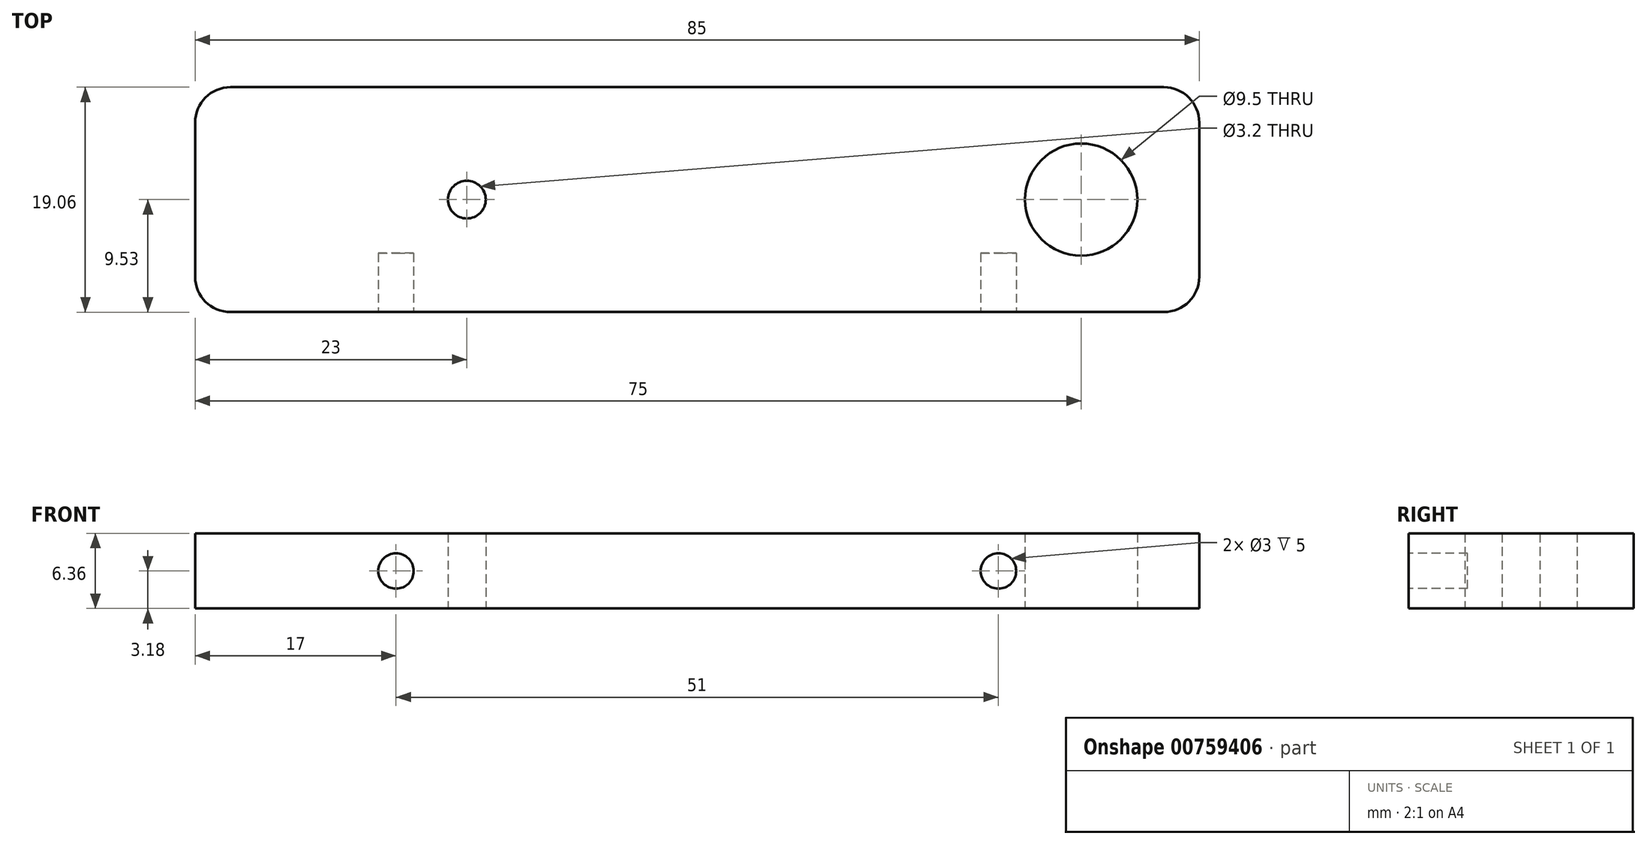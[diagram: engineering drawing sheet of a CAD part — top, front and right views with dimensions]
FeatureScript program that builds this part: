
annotation { "Feature Type Name" : "Feature", "Feature Type Description" : "" }
export const myFeature = defineFeature(function(context is Context, id is Id, definition is map)
    precondition{}
    {
        {
            var Q0;
            Q0=qCreatedBy(makeId("Top.planeOp"),FACE);
            var sketch = newSketch(context, id + "F0", { "sketchPlane" : qUnion([Q0])});
            skLineSegment(sketch, "E0.bottom", {"start": v(42.5, -9.52) * mm, "end": v(-42.5, -9.53) * mm});
            skLineSegment(sketch, "E0.top", {"start": v(42.5, 9.53) * mm, "end": v(-42.5, 9.52) * mm});
            skLineSegment(sketch, "E0.left", {"start": v(42.5, -9.52) * mm, "end": v(42.5, 9.53) * mm});
            skLineSegment(sketch, "E0.right", {"start": v(-42.5, -9.53) * mm, "end": v(-42.5, 9.52) * mm});
            skPoint(sketch, "E0.middle", {"position": v(0, 0) * mm});
            skCircle(sketch, "E1", {"center": v(32.5, 0) * mm, "radius": 4.75 * mm});
            skCircle(sketch, "E2", {"center": v(-19.5, 0) * mm, "radius": 1.6 * mm});
            skSolve(sketch);
        }
        {
            var Q0;
            Q0 = qSketchRegion(id + "F0", true);
            extrude(context, id + "F1", {"entities" : qUnion([Q0]), "endBound" : BoundingType.SYMMETRIC, "depth" : 6.35 * mm, "offsetDistance" : 25 * mm});
        }
        {
            var Q0;
            Q0=makeQuery(id+"F1.opExtrude","SWEPT_FACE",FACE,{"disambiguationData":[OSD([sQuery(id+"F0.wireOp",EDGE,"E0.bottom")])]});
            var sketch = newSketch(context, id + "F2", { "sketchPlane" : qUnion([Q0])});
            skCircle(sketch, "E3", {"center": v(-25.5, 0) * mm, "radius": 1.5 * mm});
            skCircle(sketch, "E4.MirrorC", {"center": v(25.5, 0) * mm, "radius": 1.5 * mm});
            skSolve(sketch);
        }
        {
            var Q0;
            Q0 = qSketchRegion(id + "F2", true);
            extrude(context, id + "F3", {"entities" : qUnion([Q0]), "operationType" : NewBodyOperationType.REMOVE, "oppositeDirection" : true, "depth" : 5 * mm, "offsetDistance" : 25 * mm});
        }
        {
            var Q0;
            Q0=makeQuery(id+"F1.opExtrude","SWEPT_EDGE",EDGE,{"disambiguationData":[OSD([sQuery(id+"F0.wireOp",EDGE,"E0.bottom"),sQuery(id+"F0.wireOp",EDGE,"E0.left")])]});
            var Q1;
            Q1=makeQuery(id+"F1.opExtrude","SWEPT_EDGE",EDGE,{"disambiguationData":[OSD([sQuery(id+"F0.wireOp",EDGE,"E0.top"),sQuery(id+"F0.wireOp",EDGE,"E0.left")])]});
            var Q2;
            Q2=makeQuery(id+"F1.opExtrude","SWEPT_EDGE",EDGE,{"disambiguationData":[OSD([sQuery(id+"F0.wireOp",EDGE,"E0.bottom"),sQuery(id+"F0.wireOp",EDGE,"E0.right")])]});
            var Q3;
            Q3=makeQuery(id+"F1.opExtrude","SWEPT_EDGE",EDGE,{"disambiguationData":[OSD([sQuery(id+"F0.wireOp",EDGE,"E0.top"),sQuery(id+"F0.wireOp",EDGE,"E0.right")])]});
            fillet(context, id + "F4", {"entities" : qUnion([Q0, Q1, Q2, Q3]), "radius" : 3 * mm, "tangentPropagation" : true, "allowEdgeOverflow" : false});
        }
    });
